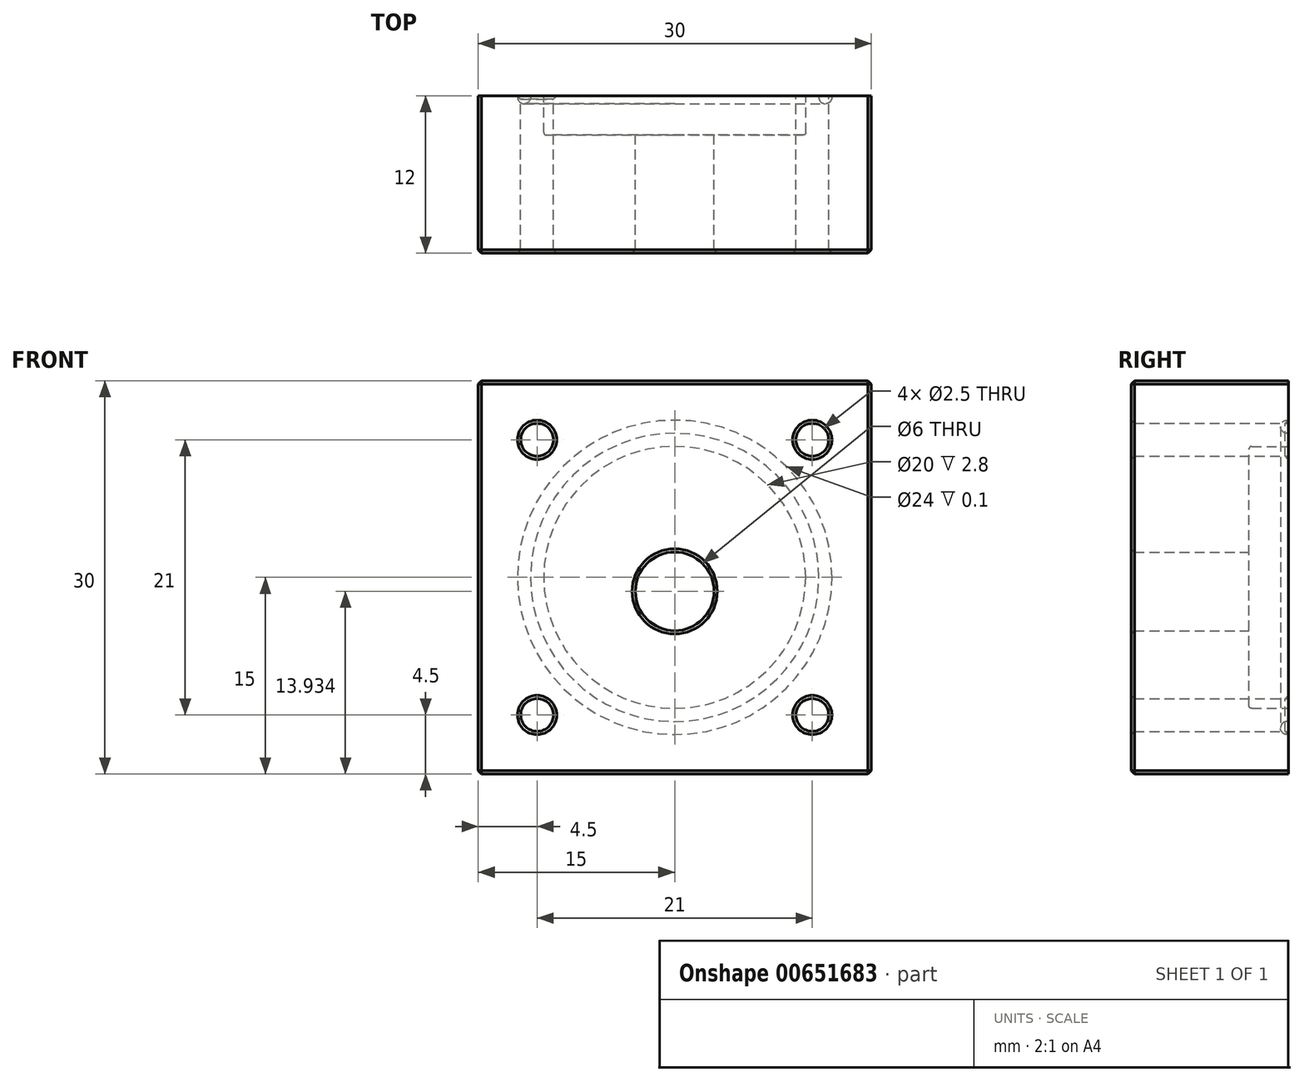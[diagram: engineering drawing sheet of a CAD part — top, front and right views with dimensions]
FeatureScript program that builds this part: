
annotation { "Feature Type Name" : "Feature", "Feature Type Description" : "" }
export const myFeature = defineFeature(function(context is Context, id is Id, definition is map)
    precondition{}
    {
        {
            var Q0;
            Q0=qCreatedBy(makeId("Front.planeOp"),FACE);
            var sketch = newSketch(context, id + "F0", { "sketchPlane" : qUnion([Q0])});
            skLineSegment(sketch, "E0.bottom", {"start": v(0, 0) * mm, "end": v(30, 0) * mm});
            skLineSegment(sketch, "E0.top", {"start": v(0, -30) * mm, "end": v(30, -30) * mm});
            skLineSegment(sketch, "E0.left", {"start": v(0, 0) * mm, "end": v(0, -30) * mm});
            skLineSegment(sketch, "E0.right", {"start": v(30, 0) * mm, "end": v(30, -30) * mm});
            skLineSegment(sketch, "E1", {"start": v(15, 0) * mm, "end": v(15, -30) * mm, "construction": true});
            skCircle(sketch, "E2", {"center": v(15, -16.07) * mm, "radius": 3 * mm});
            skCircle(sketch, "E3", {"center": v(15, -15) * mm, "radius": 10 * mm});
            skSolve(sketch);
        }
        {
            var Q0;
            Q0=makeQuery(id+"F0.imprint","IMPRINT",FACE,{"disambiguationData":[TD([[makeQuery(id+"F0.imprint","IMPRINT",EDGE,{"derivedFrom":sQuery(id+"F0.wireOp",EDGE,"E0.bottom")}),-1.0]])]});
            var Q1;
            Q1=makeQuery(id+"F0.imprint","IMPRINT",FACE,{"disambiguationData":[TD([[makeQuery(id+"F0.imprint","IMPRINT",EDGE,{"derivedFrom":sQuery(id+"F0.wireOp",EDGE,"E2")}),-1.0]])]});
            extrude(context, id + "F1", {"entities" : qUnion([Q0, Q1]), "depth" : 12 * mm, "offsetDistance" : 25 * mm});
        }
        {
            var Q0;
            Q0=makeQuery(id+"F0.imprint","IMPRINT",FACE,{"disambiguationData":[TD([[makeQuery(id+"F0.imprint","IMPRINT",EDGE,{"derivedFrom":sQuery(id+"F0.wireOp",EDGE,"E2")}),-1.0]])]});
            extrude(context, id + "F2", {"entities" : qUnion([Q0]), "operationType" : NewBodyOperationType.REMOVE, "depth" : 3 * mm, "offsetDistance" : 25 * mm});
        }
        {
            var Q0;
            Q0=makeQuery(id+"F2.boolean.opBoolean","COPY",EDGE,{"derivedFrom":makeQuery(id+"F2.opExtrude","CAP_EDGE",EDGE,{"disambiguationData":[OSD([sQuery(id+"F0.wireOp",EDGE,"E3")])],"isStart":false})});
            fillet(context, id + "F3", {"entities" : qUnion([Q0]), "radius" : 0.2 * mm, "tangentPropagation" : true, "allowEdgeOverflow" : false});
        }
        {
            var Q0;
            Q0=makeQuery(id+"F1.opExtrude","CAP_FACE",FACE,{"disambiguationData":[OSD([sQuery(id+"F0.wireOp",EDGE,"E0.bottom"),sQuery(id+"F0.wireOp",EDGE,"E0.top"),sQuery(id+"F0.wireOp",EDGE,"E0.left"),sQuery(id+"F0.wireOp",EDGE,"E0.right"),sQuery(id+"F0.wireOp",EDGE,"E2")])],"isStart":true});
            var sketch = newSketch(context, id + "F4", { "sketchPlane" : qUnion([Q0])});
            skCircle(sketch, "E4", {"center": v(-15, -15) * mm, "radius": 11 * mm});
            skCircle(sketch, "E5", {"center": v(-15, -15) * mm, "radius": 12 * mm});
            skLineSegment(sketch, "E6", {"start": v(-4.5, 0) * mm, "end": v(-4.5, -4.5) * mm, "construction": true});
            skLineSegment(sketch, "E7", {"start": v(-4.5, -4.5) * mm, "end": v(0, -4.5) * mm, "construction": true});
            skCircle(sketch, "E8", {"center": v(-4.5, -4.5) * mm, "radius": 1.25 * mm});
            skLineSegment(sketch, "E9", {"start": v(-25.5, 0) * mm, "end": v(-25.5, -4.5) * mm, "construction": true});
            skLineSegment(sketch, "E10", {"start": v(-25.5, -4.5) * mm, "end": v(-30, -4.5) * mm, "construction": true});
            skLineSegment(sketch, "E11", {"start": v(-30, -25.5) * mm, "end": v(-25.5, -25.5) * mm, "construction": true});
            skLineSegment(sketch, "E12", {"start": v(-4.5, -30) * mm, "end": v(-4.5, -25.5) * mm, "construction": true});
            skLineSegment(sketch, "E13", {"start": v(-4.5, -25.5) * mm, "end": v(0, -25.5) * mm, "construction": true});
            skLineSegment(sketch, "E14", {"start": v(-25.5, -25.5) * mm, "end": v(-25.5, -30) * mm, "construction": true});
            skCircle(sketch, "E15", {"center": v(-25.5, -4.5) * mm, "radius": 1.25 * mm});
            skCircle(sketch, "E16", {"center": v(-25.5, -25.5) * mm, "radius": 1.25 * mm});
            skCircle(sketch, "E17", {"center": v(-4.5, -25.5) * mm, "radius": 1.25 * mm});
            skSolve(sketch);
        }
        {
            var Q0;
            Q0=makeQuery(id+"F4.imprint","IMPRINT",FACE,{"disambiguationData":[TD([[makeQuery(id+"F4.imprint","IMPRINT",EDGE,{"derivedFrom":sQuery(id+"F4.wireOp",EDGE,"E4")}),-1.0]])]});
            extrude(context, id + "F5", {"entities" : qUnion([Q0]), "operationType" : NewBodyOperationType.REMOVE, "oppositeDirection" : true, "depth" : .6 * mm, "offsetDistance" : 25 * mm});
        }
        {
            var Q0;
            Q0=makeQuery(id+"F5.boolean.opBoolean","COPY",EDGE,{"derivedFrom":makeQuery(id+"F5.opExtrude","CAP_EDGE",EDGE,{"disambiguationData":[OSD([sQuery(id+"F4.wireOp",EDGE,"E4")])],"isStart":false})});
            var Q1;
            Q1=makeQuery(id+"F5.boolean.opBoolean","COPY",EDGE,{"derivedFrom":makeQuery(id+"F5.opExtrude","CAP_EDGE",EDGE,{"disambiguationData":[OSD([sQuery(id+"F4.wireOp",EDGE,"E5")])],"isStart":false})});
            fillet(context, id + "F6", {"entities" : qUnion([Q0, Q1]), "radius" : .5 * mm, "tangentPropagation" : true, "allowEdgeOverflow" : false});
        }
        {
            var Q0;
            Q0=makeQuery(id+"F4.imprint","IMPRINT",FACE,{"disambiguationData":[TD([[makeQuery(id+"F4.imprint","IMPRINT",EDGE,{"derivedFrom":sQuery(id+"F4.wireOp",EDGE,"E8")}),1.0]])]});
            var Q1;
            Q1=makeQuery(id+"F4.imprint","IMPRINT",FACE,{"disambiguationData":[TD([[makeQuery(id+"F4.imprint","IMPRINT",EDGE,{"derivedFrom":sQuery(id+"F4.wireOp",EDGE,"E15")}),1.0]])]});
            var Q2;
            Q2=makeQuery(id+"F4.imprint","IMPRINT",FACE,{"disambiguationData":[TD([[makeQuery(id+"F4.imprint","IMPRINT",EDGE,{"derivedFrom":sQuery(id+"F4.wireOp",EDGE,"E16")}),1.0]])]});
            var Q3;
            Q3=makeQuery(id+"F4.imprint","IMPRINT",FACE,{"disambiguationData":[TD([[makeQuery(id+"F4.imprint","IMPRINT",EDGE,{"derivedFrom":sQuery(id+"F4.wireOp",EDGE,"E17")}),1.0]])]});
            extrude(context, id + "F7", {"entities" : qUnion([Q0, Q1, Q2, Q3]), "operationType" : NewBodyOperationType.REMOVE, "oppositeDirection" : true, "depth" : 25 * mm, "offsetDistance" : 25 * mm});
        }
        {
            var Q0;
            Q0=makeQuery(id+"F1.opExtrude","CAP_FACE",FACE,{"disambiguationData":[OSD([sQuery(id+"F0.wireOp",EDGE,"E0.bottom"),sQuery(id+"F0.wireOp",EDGE,"E0.top"),sQuery(id+"F0.wireOp",EDGE,"E0.left"),sQuery(id+"F0.wireOp",EDGE,"E0.right"),sQuery(id+"F0.wireOp",EDGE,"E2")])],"isStart":false});
            var Q1;
            Q1=makeQuery(id+"F1.opExtrude","SWEPT_EDGE",EDGE,{"disambiguationData":[OSD([sQuery(id+"F0.wireOp",EDGE,"E0.bottom"),sQuery(id+"F0.wireOp",EDGE,"E0.right")])]});
            var Q2;
            Q2=makeQuery(id+"F1.opExtrude","SWEPT_EDGE",EDGE,{"disambiguationData":[OSD([sQuery(id+"F0.wireOp",EDGE,"E0.bottom"),sQuery(id+"F0.wireOp",EDGE,"E0.left")])]});
            var Q3;
            Q3=makeQuery(id+"F1.opExtrude","SWEPT_EDGE",EDGE,{"disambiguationData":[OSD([sQuery(id+"F0.wireOp",EDGE,"E0.top"),sQuery(id+"F0.wireOp",EDGE,"E0.right")])]});
            var Q4;
            Q4=makeQuery(id+"F1.opExtrude","SWEPT_EDGE",EDGE,{"disambiguationData":[OSD([sQuery(id+"F0.wireOp",EDGE,"E0.top"),sQuery(id+"F0.wireOp",EDGE,"E0.left")])]});
            var Q5;
            Q5=makeQuery(id+"F7.boolean.opBoolean","COPY",FACE,{"derivedFrom":makeQuery(id+"F7.opExtrude","SWEPT_FACE",FACE,{"disambiguationData":[OSD([sQuery(id+"F4.wireOp",EDGE,"E8")])]})});
            var Q6;
            Q6=makeQuery(id+"F7.boolean.opBoolean","COPY",EDGE,{"derivedFrom":makeQuery(id+"F7.opExtrude","CAP_EDGE",EDGE,{"disambiguationData":[OSD([sQuery(id+"F4.wireOp",EDGE,"E16")])],"isStart":true})});
            var Q7;
            Q7=makeQuery(id+"F7.boolean.opBoolean","COPY",FACE,{"derivedFrom":makeQuery(id+"F7.opExtrude","SWEPT_FACE",FACE,{"disambiguationData":[OSD([sQuery(id+"F4.wireOp",EDGE,"E17")])]})});
            var Q8;
            Q8=makeQuery(id+"F7.boolean.opBoolean","COPY",EDGE,{"derivedFrom":makeQuery(id+"F7.opExtrude","CAP_EDGE",EDGE,{"disambiguationData":[OSD([sQuery(id+"F4.wireOp",EDGE,"E15")])],"isStart":true})});
            chamfer(context, id + "F8", {"entities" : qUnion([Q0, Q1, Q2, Q3, Q4, Q5, Q6, Q7, Q8]), "width" : .25 * mm, "tangentPropagation" : true});
        }
    });
